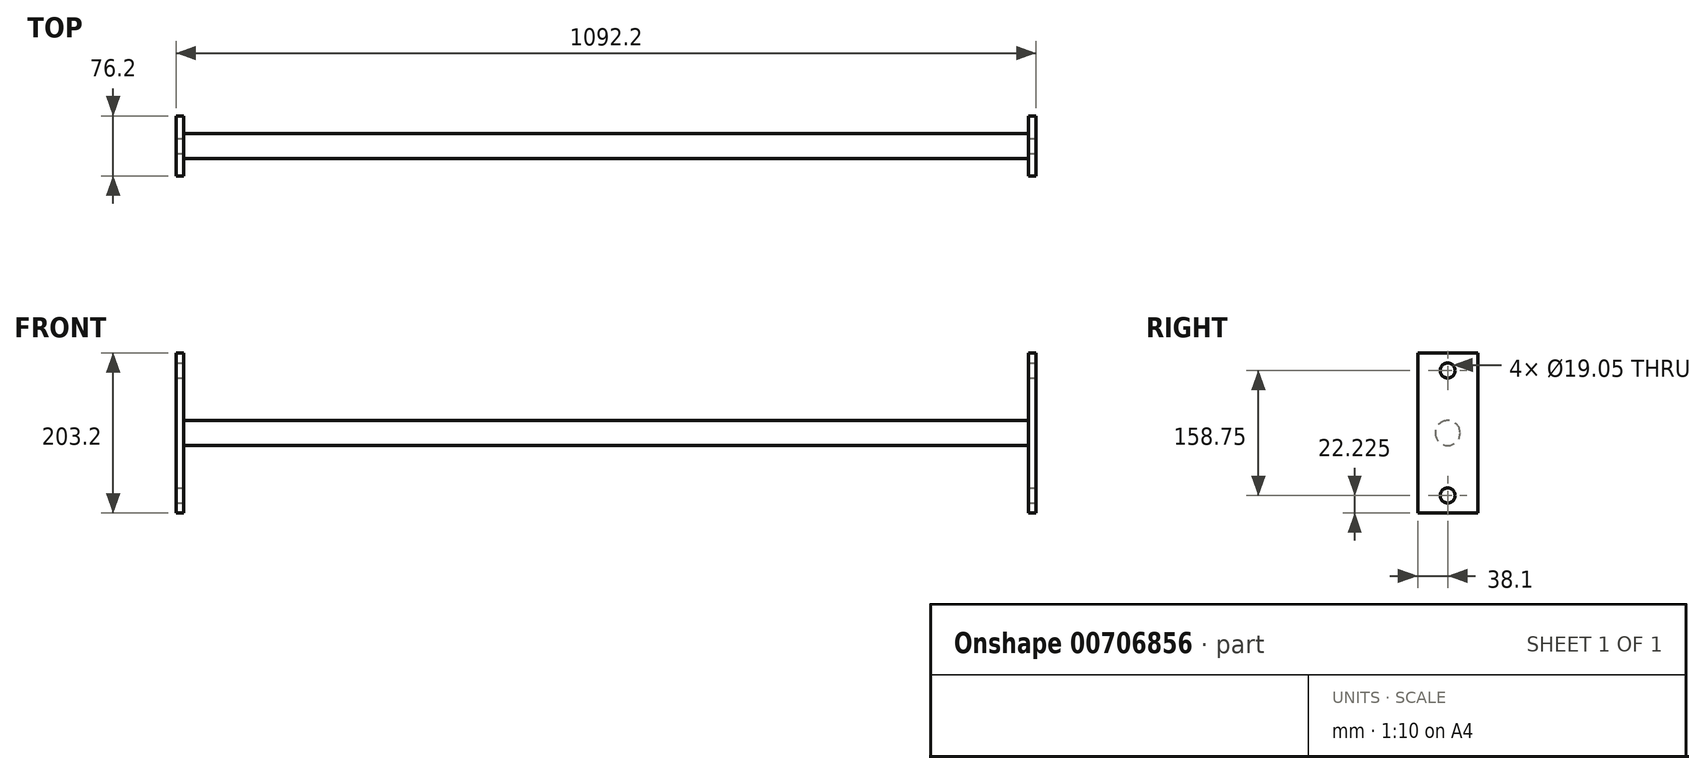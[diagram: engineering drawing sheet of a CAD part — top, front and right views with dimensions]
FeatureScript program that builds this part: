
annotation { "Feature Type Name" : "Feature", "Feature Type Description" : "" }
export const myFeature = defineFeature(function(context is Context, id is Id, definition is map)
    precondition{}
    {
        {
            var Q0;
            Q0=qCreatedBy(makeId("Front.planeOp"),FACE);
            var sketch = newSketch(context, id + "F0", { "sketchPlane" : qUnion([Q0])});
            skLineSegment(sketch, "E0.bottom", {"start": v(-546.1, 101.6) * mm, "end": v(-536.58, 101.6) * mm});
            skLineSegment(sketch, "E0.top", {"start": v(-546.1, -101.6) * mm, "end": v(-536.58, -101.6) * mm});
            skLineSegment(sketch, "E0.left", {"start": v(-546.1, 101.6) * mm, "end": v(-546.1, -101.6) * mm});
            skLineSegment(sketch, "E0.right", {"start": v(-536.58, 101.6) * mm, "end": v(-536.58, -101.6) * mm});
            skLineSegment(sketch, "E1.MirrorCS", {"start": v(536.58, 101.6) * mm, "end": v(536.58, -101.6) * mm});
            skLineSegment(sketch, "E2.MirrorCS", {"start": v(546.1, 101.6) * mm, "end": v(546.1, -101.6) * mm});
            skLineSegment(sketch, "E3.MirrorCS", {"start": v(546.1, 101.6) * mm, "end": v(536.58, 101.6) * mm});
            skLineSegment(sketch, "E4.MirrorCS", {"start": v(546.1, -101.6) * mm, "end": v(536.58, -101.6) * mm});
            skSolve(sketch);
        }
        {
            var Q0;
            Q0=qSketchRegion(id+"F0",true);
            extrude(context, id + "F1", {"entities" : qUnion([Q0]), "depth" : 38.1 * mm, "offsetDistance" : 25 * mm, "hasSecondDirection" : true, "secondDirectionOppositeDirection" : true, "secondDirectionDepth" : 38.1 * mm});
        }
        {
            var Q0;
            Q0=qCreatedBy(makeId("Right.planeOp"),FACE);
            var sketch = newSketch(context, id + "F2", { "sketchPlane" : qUnion([Q0])});
            skCircle(sketch, "E5", {"center": v(0, 0) * mm, "radius": 15.88 * mm});
            skSolve(sketch);
        }
        {
            var Q0;
            Q0=qSketchRegion(id+"F2",true);
            extrude(context, id + "F3", {"entities" : qUnion([Q0]), "endBound" : BoundingType.UP_TO_NEXT, "depth" : 25.4 * mm, "offsetDistance" : 25.4 * mm, "hasSecondDirection" : true, "secondDirectionBound" : SecondDirectionBoundingType.UP_TO_NEXT, "secondDirectionOppositeDirection" : true, "secondDirectionDepth" : 25.4 * mm});
        }
        {
            var Q0;
            Q0=makeQuery(id+"F1.opExtrude","SWEPT_FACE",FACE,{"disambiguationData":[OSD([sQuery(id+"F0.wireOp",EDGE,"E2.MirrorCS")])]});
            var sketch = newSketch(context, id + "F4", { "sketchPlane" : qUnion([Q0])});
            skCircle(sketch, "E6", {"center": v(0, -79.37) * mm, "radius": 9.52 * mm});
            skCircle(sketch, "E7", {"center": v(0, 79.38) * mm, "radius": 9.52 * mm});
            skSolve(sketch);
        }
        {
            var Q0;
            Q0=qSketchRegion(id+"F4",true);
            extrude(context, id + "F5", {"entities" : qUnion([Q0]), "operationType" : NewBodyOperationType.REMOVE, "endBound" : BoundingType.THROUGH_ALL, "oppositeDirection" : true, "depth" : 25.4 * mm, "offsetDistance" : 25.4 * mm});
        }
    });
